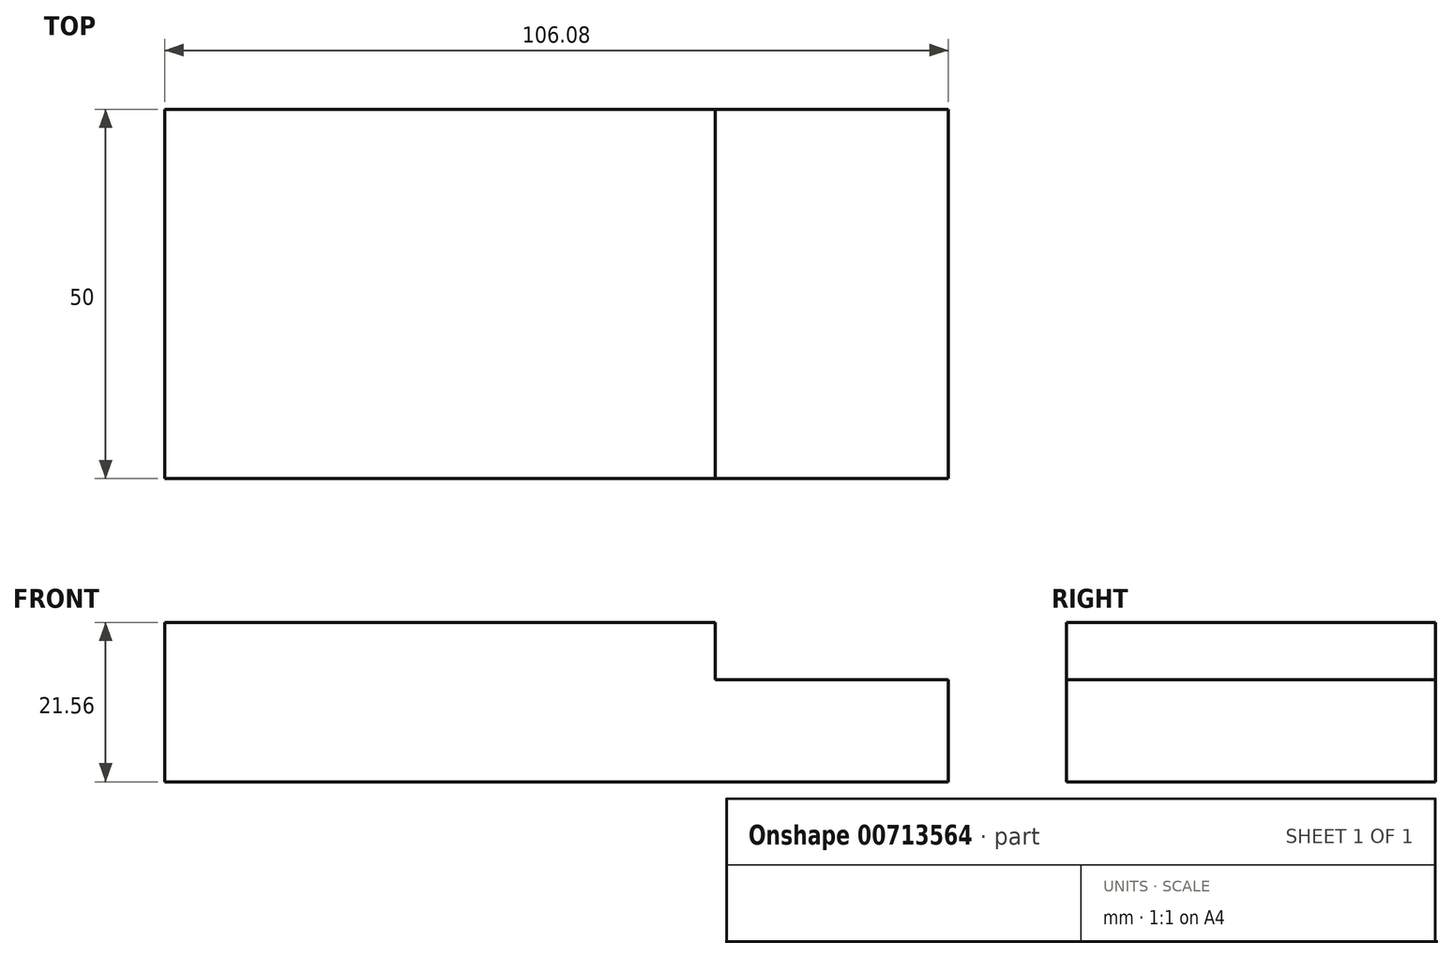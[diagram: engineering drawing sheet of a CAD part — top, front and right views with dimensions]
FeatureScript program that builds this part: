
annotation { "Feature Type Name" : "Feature", "Feature Type Description" : "" }
export const myFeature = defineFeature(function(context is Context, id is Id, definition is map)
    precondition{}
    {
        {
            var Q0;
            Q0=qCreatedBy(makeId("Front.planeOp"),FACE);
            var sketch = newSketch(context, id + "F0", { "sketchPlane" : qUnion([Q0])});
            skLineSegment(sketch, "E0.bottom", {"start": v(53.04, -10.78) * mm, "end": v(-53.04, -10.78) * mm});
            skLineSegment(sketch, "E0.top", {"start": v(53.04, 10.78) * mm, "end": v(-53.04, 10.78) * mm});
            skLineSegment(sketch, "E0.left", {"start": v(53.04, -10.78) * mm, "end": v(53.04, 10.78) * mm});
            skLineSegment(sketch, "E0.right", {"start": v(-53.04, -10.78) * mm, "end": v(-53.04, 10.78) * mm});
            skPoint(sketch, "E0.middle", {"position": v(0, 0) * mm});
            skSolve(sketch);
        }
        {
            var Q0;
            Q0=makeQuery(id+"F0.imprint","IMPRINT",FACE,{"disambiguationData":[TD([[makeQuery(id+"F0.imprint","IMPRINT",EDGE,{"derivedFrom":sQuery(id+"F0.wireOp",EDGE,"E0.bottom")}),-1.0]])]});
            extrude(context, id + "F1", {"entities" : qUnion([Q0]), "oppositeDirection" : true, "depth" : 50 * mm, "offsetDistance" : 25.4 * mm});
        }
        {
            var Q0;
            Q0=makeQuery(id+"F1.opExtrude","CAP_FACE",FACE,{"disambiguationData":[OSD([sQuery(id+"F0.wireOp",EDGE,"E0.bottom"),sQuery(id+"F0.wireOp",EDGE,"E0.top"),sQuery(id+"F0.wireOp",EDGE,"E0.left"),sQuery(id+"F0.wireOp",EDGE,"E0.right")])],"isStart":true});
            var sketch = newSketch(context, id + "F2", { "sketchPlane" : qUnion([Q0])});
            skLineSegment(sketch, "E1.bottom", {"start": v(53.04, 10.78) * mm, "end": v(21.46, 10.78) * mm});
            skLineSegment(sketch, "E1.top", {"start": v(53.04, 3.04) * mm, "end": v(21.46, 3.04) * mm});
            skLineSegment(sketch, "E1.left", {"start": v(53.04, 10.78) * mm, "end": v(53.04, 3.04) * mm});
            skLineSegment(sketch, "E1.right", {"start": v(21.46, 10.78) * mm, "end": v(21.46, 3.04) * mm});
            skSolve(sketch);
        }
        {
            var Q0;
            Q0 = qSketchRegion(id + "F2", true);
            var Q1;
            Q1=makeQuery(id+"F2.imprint","IMPRINT",FACE,{"disambiguationData":[TD([[makeQuery(id+"F2.imprint","IMPRINT",EDGE,{"derivedFrom":sQuery(id+"F2.wireOp",EDGE,"E1.bottom")}),1.0]])]});
            extrude(context, id + "F3", {"entities" : qUnion([Q0, Q1]), "operationType" : NewBodyOperationType.REMOVE, "oppositeDirection" : true, "depth" : 50 * mm, "offsetDistance" : 25.4 * mm});
        }
    });
